# Revit family: HUNTER-RZWS-18
name_source: partatom
category: Sprinklers
revit_build: Autodesk Revit 2017 (Build: 20160225_1515(x64)
units: mm (PartAtom-declared; Revit-internal decimal feet)

## family parameters
Always vertical = Yes
Cut with Voids When Loaded = No
Maintain Annotation Orientation = No
OmniClass Number = 23.11.27.15.11.11
OmniClass Title = Installed Sprinkler Heads
Part Type = Normal
Room Calculation Point = No
Round Connector Dimension = Use Diameter
Shared = Yes
Work Plane-Based = No

## types (4) — shared parameters
Assembly Code = G2050700
Body Height = 450 mm  [stored 1.47638 ft]
Body Material = Hunter® ABS Plastic
Connection_Dia = 15 mm  [stored 0.0492126 ft]
Diameter = 15 mm
Exposed Diameter = 76 mm
Inlet Size = 1/2'' NPT
Keynote = 32 84 13
Manufacturer = Hunter® Industries
Operating Pressure = 280.0 kPa
Pressure = 280.0 kPa
RZWS Body = RZWS-18
Show 2D Symbol = Yes
Show Water Spray = Yes
Type Comments = Root Zone Watering System
Type Image = <None>
URL = https://www.hunterindustries.com
Water = Water
zero-valued in all types: K-Factor

## per-type parameters (varying)
| type | Bubbler Nozzle | Check Valve | Description |
| RZWS-18-25-CV | 25 Bubbler | Check Valve included (HCV) | 18" Root Zone Watering System with bubbler 25 (0.9 l/min) and Check Valve |
| RZWS-18-50-CV | 50 Bubbler | Check Valve included (HCV) | 18" Root Zone Watering System with bubbler 50 (1.9 l/min) and Check Valve |
| RZWS-18-50 | 50 Bubbler |  | 18" Root Zone Watering System with bubbler 50 (1.9 l/min) |
| RZWS-18-25 | 25 Bubbler |  | 18" Root Zone Watering System with bubbler 25 (0.9 l/min) |

note: column(s) folded — value = type name in every type: Model

note: [stored X ft] marks values corroborated as IEEE doubles in the binary element streams (Revit-internal decimal feet)

## geometry (parser evidence)
native form markers: Sweep x11
no freeform markers — native parametric forms only
